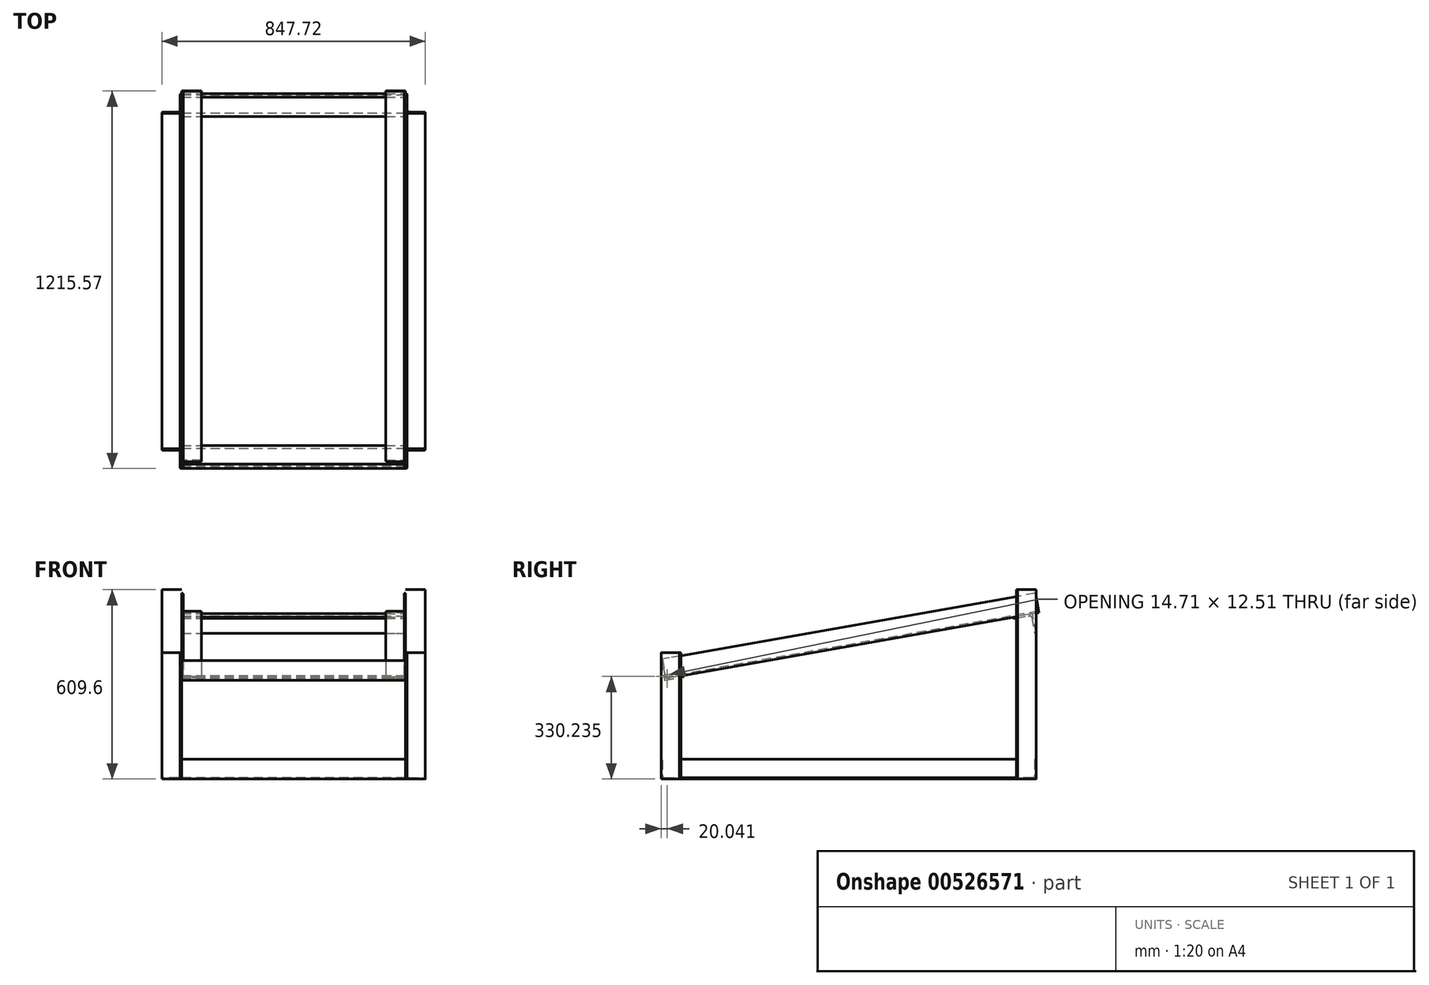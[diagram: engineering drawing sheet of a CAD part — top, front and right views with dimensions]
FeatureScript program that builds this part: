
annotation { "Feature Type Name" : "Feature", "Feature Type Description" : "" }
export const myFeature = defineFeature(function(context is Context, id is Id, definition is map)
    precondition{}
    {
        {
            var Q0;
            Q0=qCreatedBy(makeId("Right.planeOp"),FACE);
            var sketch = newSketch(context, id + "F0", { "sketchPlane" : qUnion([Q0])});
            skLineSegment(sketch, "E0.bottom", {"start": v(0, 0) * mm, "end": v(63.5, 0) * mm});
            skLineSegment(sketch, "E0.top", {"start": v(0, 406.4) * mm, "end": v(63.5, 406.4) * mm});
            skLineSegment(sketch, "E0.left", {"start": v(0, 0) * mm, "end": v(0, 406.4) * mm});
            skLineSegment(sketch, "E0.right", {"start": v(63.5, 0) * mm, "end": v(63.5, 406.4) * mm});
            skLineSegment(sketch, "E1.bottom", {"start": v(1143, 0) * mm, "end": v(1206.5, 0) * mm});
            skLineSegment(sketch, "E1.top", {"start": v(1143, 609.6) * mm, "end": v(1206.5, 609.6) * mm});
            skLineSegment(sketch, "E1.left", {"start": v(1143, 0) * mm, "end": v(1143, 609.6) * mm});
            skLineSegment(sketch, "E1.right", {"start": v(1206.5, 0) * mm, "end": v(1206.5, 609.6) * mm});
            skLineSegment(sketch, "E2", {"start": v(66.78, 468.54) * mm, "end": v(1142.38, 658.2) * mm, "construction": true});
            skLineSegment(sketch, "E3", {"start": v(66.78, 468.54) * mm, "end": v(-8.2, 893.78) * mm, "construction": true});
            skLineSegment(sketch, "E4", {"start": v(-8.2, 893.78) * mm, "end": v(1067.4, 1083.44) * mm, "construction": true});
            skLineSegment(sketch, "E5", {"start": v(1067.4, 1083.44) * mm, "end": v(1142.38, 658.2) * mm, "construction": true});
            skLineSegment(sketch, "E6", {"start": v(21.14, 325.08) * mm, "end": v(1234.33, 539) * mm});
            skLineSegment(sketch, "E7", {"start": v(1234.33, 539) * mm, "end": v(1208.97, 682.83) * mm});
            skLineSegment(sketch, "E8", {"start": v(1208.97, 682.83) * mm, "end": v(-4.22, 468.92) * mm});
            skLineSegment(sketch, "E9", {"start": v(-4.22, 468.92) * mm, "end": v(21.14, 325.08) * mm});
            skLineSegment(sketch, "E10", {"start": v(5.24, 378.7) * mm, "end": v(13.79, 330.24) * mm});
            skLineSegment(sketch, "E11", {"start": v(21.14, 325.08) * mm, "end": v(69.6, 333.63) * mm});
            skLineSegment(sketch, "E12", {"start": v(73.29, 331.05) * mm, "end": v(73.56, 329.5) * mm});
            skLineSegment(sketch, "E13", {"start": v(73.56, 329.5) * mm, "end": v(11.03, 318.46) * mm});
            skLineSegment(sketch, "E14", {"start": v(11.03, 318.46) * mm, "end": v(0, 381) * mm});
            skLineSegment(sketch, "E15", {"start": v(0, 381) * mm, "end": v(1.56, 381.28) * mm});
            skPoint(sketch, "E16.visualSharp", {"position": v(14.89, 323.98) * mm});
            skArc(sketch, "E16.filletArc", {"start": v(13.79, 330.24) * mm, "mid": v(16.4, 326.14) * mm, "end": v(21.14, 325.08) * mm});
            skPoint(sketch, "E17.visualSharp", {"position": v(72.73, 334.18) * mm});
            skArc(sketch, "E17.filletArc", {"start": v(73.29, 331.05) * mm, "mid": v(71.98, 333.1) * mm, "end": v(69.6, 333.63) * mm});
            skPoint(sketch, "E18.visualSharp", {"position": v(4.7, 381.83) * mm});
            skArc(sketch, "E18.filletArc", {"start": v(5.24, 378.7) * mm, "mid": v(3.94, 380.75) * mm, "end": v(1.56, 381.28) * mm});
            skLineSegment(sketch, "E19", {"start": v(1132.94, 521.12) * mm, "end": v(1195.47, 532.15) * mm});
            skLineSegment(sketch, "E20", {"start": v(1195.47, 532.15) * mm, "end": v(1206.5, 469.62) * mm});
            skLineSegment(sketch, "E21", {"start": v(1206.5, 469.62) * mm, "end": v(1204.94, 469.34) * mm});
            skLineSegment(sketch, "E22", {"start": v(1201.26, 471.92) * mm, "end": v(1192.71, 520.38) * mm});
            skLineSegment(sketch, "E23", {"start": v(1185.36, 525.53) * mm, "end": v(1136.9, 516.99) * mm});
            skLineSegment(sketch, "E24", {"start": v(1133.21, 519.56) * mm, "end": v(1132.94, 521.12) * mm});
            skPoint(sketch, "E25.visualSharp", {"position": v(1133.77, 516.43) * mm});
            skArc(sketch, "E25.filletArc", {"start": v(1133.21, 519.56) * mm, "mid": v(1134.52, 517.51) * mm, "end": v(1136.9, 516.99) * mm});
            skPoint(sketch, "E26.visualSharp", {"position": v(1201.8, 468.79) * mm});
            skArc(sketch, "E26.filletArc", {"start": v(1201.26, 471.92) * mm, "mid": v(1202.56, 469.87) * mm, "end": v(1204.94, 469.34) * mm});
            skPoint(sketch, "E27.visualSharp", {"position": v(1191.61, 526.63) * mm});
            skArc(sketch, "E27.filletArc", {"start": v(1192.71, 520.38) * mm, "mid": v(1190.1, 524.48) * mm, "end": v(1185.36, 525.53) * mm});
            skLineSegment(sketch, "E28", {"start": v(-4.22, 468.92) * mm, "end": v(-16.35, 537.7) * mm, "construction": true});
            skLineSegment(sketch, "E29", {"start": v(-16.35, 537.7) * mm, "end": v(52.44, 549.83) * mm, "construction": true});
            skLineSegment(sketch, "E30", {"start": v(1208.97, 682.83) * mm, "end": v(1196.84, 751.62) * mm, "construction": true});
            skLineSegment(sketch, "E31", {"start": v(1196.84, 751.62) * mm, "end": v(1128.05, 739.5) * mm, "construction": true});
            skLineSegment(sketch, "E32", {"start": v(63.5, 0) * mm, "end": v(1143, 0) * mm, "construction": true});
            skLineSegment(sketch, "E33", {"start": v(603.25, 0) * mm, "end": v(603.25, 427.73) * mm, "construction": true});
            skSolve(sketch);
        }
        {
            var Q0;
            Q0=qCreatedBy(makeId("Top.planeOp"),FACE);
            var sketch = newSketch(context, id + "F1", { "sketchPlane" : qUnion([Q0])});
            skLineSegment(sketch, "E34", {"start": v(-355.6, 0) * mm, "end": v(355.6, 0) * mm, "construction": true});
            skLineSegment(sketch, "E35", {"start": v(360.36, 0) * mm, "end": v(360.36, 63.5) * mm});
            skLineSegment(sketch, "E36", {"start": v(360.36, 63.5) * mm, "end": v(423.86, 63.5) * mm});
            skLineSegment(sketch, "E37", {"start": v(423.86, 63.5) * mm, "end": v(423.86, 61.91) * mm});
            skLineSegment(sketch, "E38", {"start": v(420.69, 58.74) * mm, "end": v(371.48, 58.74) * mm});
            skLineSegment(sketch, "E39", {"start": v(365.13, 52.39) * mm, "end": v(365.13, 3.17) * mm});
            skLineSegment(sketch, "E40", {"start": v(361.95, 0) * mm, "end": v(360.36, 0) * mm});
            skPoint(sketch, "E41.visualSharp", {"position": v(365.13, 58.74) * mm});
            skArc(sketch, "E41.filletArc", {"start": v(371.48, 58.74) * mm, "mid": v(366.98, 56.88) * mm, "end": v(365.13, 52.39) * mm});
            skPoint(sketch, "E42.visualSharp", {"position": v(423.86, 58.74) * mm});
            skArc(sketch, "E42.filletArc", {"start": v(420.69, 58.74) * mm, "mid": v(422.93, 59.67) * mm, "end": v(423.86, 61.91) * mm});
            skPoint(sketch, "E43.visualSharp", {"position": v(365.13, 0) * mm});
            skArc(sketch, "E43.filletArc", {"start": v(361.95, 0) * mm, "mid": v(364.2, 0.93) * mm, "end": v(365.13, 3.17) * mm});
            skLineSegment(sketch, "E44", {"start": v(0, 603.25) * mm, "end": v(711.2, 603.25) * mm, "construction": true});
            skLineSegment(sketch, "E45.MirrorCS", {"start": v(361.95, 1206.5) * mm, "end": v(360.36, 1206.5) * mm});
            skLineSegment(sketch, "E46.MirrorCS", {"start": v(423.86, 1143) * mm, "end": v(423.86, 1144.59) * mm});
            skArc(sketch, "E47.MirrorCS", {"start": v(420.69, 1147.76) * mm, "mid": v(422.93, 1146.83) * mm, "end": v(423.86, 1144.59) * mm});
            skArc(sketch, "E48.MirrorCS", {"start": v(361.95, 1206.5) * mm, "mid": v(364.2, 1205.57) * mm, "end": v(365.13, 1203.33) * mm});
            skArc(sketch, "E49.MirrorCS", {"start": v(371.48, 1147.76) * mm, "mid": v(366.98, 1149.62) * mm, "end": v(365.13, 1154.11) * mm});
            skLineSegment(sketch, "E50.MirrorCS", {"start": v(365.13, 1154.11) * mm, "end": v(365.13, 1203.33) * mm});
            skLineSegment(sketch, "E51.MirrorCS", {"start": v(420.69, 1147.76) * mm, "end": v(371.48, 1147.76) * mm});
            skLineSegment(sketch, "E52.MirrorCS", {"start": v(360.36, 1206.5) * mm, "end": v(360.36, 1143) * mm});
            skLineSegment(sketch, "E53.MirrorCS", {"start": v(360.36, 1143) * mm, "end": v(423.86, 1143) * mm});
            skPoint(sketch, "E54.MirrorP", {"position": v(365.13, 1147.76) * mm});
            skPoint(sketch, "E55.MirrorP", {"position": v(423.86, 1147.76) * mm});
            skPoint(sketch, "E56.MirrorP", {"position": v(365.13, 1206.5) * mm});
            skLineSegment(sketch, "E57.MirrorCS", {"start": v(-361.95, 1206.5) * mm, "end": v(-360.36, 1206.5) * mm});
            skLineSegment(sketch, "E58.MirrorCS", {"start": v(-423.86, 1143) * mm, "end": v(-423.86, 1144.59) * mm});
            skArc(sketch, "E59.MirrorCS", {"start": v(-361.95, 1206.5) * mm, "mid": v(-364.2, 1205.57) * mm, "end": v(-365.13, 1203.33) * mm});
            skArc(sketch, "E60.MirrorCS", {"start": v(-420.69, 1147.76) * mm, "mid": v(-422.93, 1146.83) * mm, "end": v(-423.86, 1144.59) * mm});
            skArc(sketch, "E61.MirrorCS", {"start": v(-371.48, 1147.76) * mm, "mid": v(-366.98, 1149.62) * mm, "end": v(-365.13, 1154.11) * mm});
            skPoint(sketch, "E62.MirrorP", {"position": v(-423.86, 1147.76) * mm});
            skLineSegment(sketch, "E63.MirrorCS", {"start": v(-420.69, 1147.76) * mm, "end": v(-371.48, 1147.76) * mm});
            skLineSegment(sketch, "E64.MirrorCS", {"start": v(-360.36, 1143) * mm, "end": v(-423.86, 1143) * mm});
            skPoint(sketch, "E65.MirrorP", {"position": v(-365.13, 1147.76) * mm});
            skPoint(sketch, "E66.MirrorP", {"position": v(-365.13, 1206.5) * mm});
            skLineSegment(sketch, "E67.MirrorCS", {"start": v(-365.13, 1154.11) * mm, "end": v(-365.13, 1203.33) * mm});
            skLineSegment(sketch, "E68.MirrorCS", {"start": v(-360.36, 1206.5) * mm, "end": v(-360.36, 1143) * mm});
            skLineSegment(sketch, "E69.MirrorCS", {"start": v(-361.95, 0) * mm, "end": v(-360.36, 0) * mm});
            skLineSegment(sketch, "E70.MirrorCS", {"start": v(-423.86, 63.5) * mm, "end": v(-423.86, 61.91) * mm});
            skArc(sketch, "E71.MirrorCS", {"start": v(-420.69, 58.74) * mm, "mid": v(-422.93, 59.67) * mm, "end": v(-423.86, 61.91) * mm});
            skArc(sketch, "E72.MirrorCS", {"start": v(-361.95, 0) * mm, "mid": v(-364.2, 0.93) * mm, "end": v(-365.13, 3.17) * mm});
            skArc(sketch, "E73.MirrorCS", {"start": v(-371.48, 58.74) * mm, "mid": v(-366.98, 56.88) * mm, "end": v(-365.13, 52.39) * mm});
            skLineSegment(sketch, "E74.MirrorCS", {"start": v(-365.13, 52.39) * mm, "end": v(-365.13, 3.17) * mm});
            skLineSegment(sketch, "E75.MirrorCS", {"start": v(-420.69, 58.74) * mm, "end": v(-371.48, 58.74) * mm});
            skLineSegment(sketch, "E76.MirrorCS", {"start": v(-360.36, 0) * mm, "end": v(-360.36, 63.5) * mm});
            skLineSegment(sketch, "E77.MirrorCS", {"start": v(-360.36, 63.5) * mm, "end": v(-423.86, 63.5) * mm});
            skPoint(sketch, "E78.MirrorP", {"position": v(-365.13, 58.74) * mm});
            skPoint(sketch, "E79.MirrorP", {"position": v(-423.86, 58.74) * mm});
            skPoint(sketch, "E80.MirrorP", {"position": v(-365.13, 0) * mm});
            skSolve(sketch);
        }
        {
            var Q0;
            Q0=makeQuery(id+"F1.imprint","IMPRINT",FACE,{"disambiguationData":[TD([[makeQuery(id+"F1.imprint","IMPRINT",EDGE,{"derivedFrom":sQuery(id+"F1.wireOp",EDGE,"E69.MirrorCS")}),1.0]])]});
            var Q1;
            Q1=makeQuery(id+"F1.imprint","IMPRINT",FACE,{"disambiguationData":[TD([[makeQuery(id+"F1.imprint","IMPRINT",EDGE,{"derivedFrom":sQuery(id+"F1.wireOp",EDGE,"E35")}),-1.0]])]});
            extrude(context, id + "F2", {"entities" : qUnion([Q0, Q1]), "depth" : 406.4 * mm, "offsetDistance" : 25.4 * mm});
        }
        {
            var Q0;
            Q0=makeQuery(id+"F1.imprint","IMPRINT",FACE,{"disambiguationData":[TD([[makeQuery(id+"F1.imprint","IMPRINT",EDGE,{"derivedFrom":sQuery(id+"F1.wireOp",EDGE,"E57.MirrorCS")}),-1.0]])]});
            var Q1;
            Q1=makeQuery(id+"F1.imprint","IMPRINT",FACE,{"disambiguationData":[TD([[makeQuery(id+"F1.imprint","IMPRINT",EDGE,{"derivedFrom":sQuery(id+"F1.wireOp",EDGE,"E45.MirrorCS")}),1.0]])]});
            extrude(context, id + "F3", {"entities" : qUnion([Q0, Q1]), "depth" : 609.6 * mm, "offsetDistance" : 25.4 * mm});
        }
        {
            var Q0;
            Q0=makeQuery(id+"F0.imprint","IMPRINT",FACE,{"disambiguationData":[TD([[makeQuery(id+"F0.imprint","IMPRINT",EDGE,{"derivedFrom":sQuery(id+"F0.wireOp",EDGE,"E10")}),-1.0]])]});
            var Q1;
            {var subQ0=sQuery(id+"F0.wireOp",EDGE,"E20");Q1=makeQuery(id+"F0.imprint","IMPRINT",FACE,{"disambiguationData":[TD([[makeQuery(id+"F0.imprint","IMPRINT",EDGE,{"derivedFrom":subQ0}),-1.0]])]});}
            var Q2;
            {var subQ1=sQuery(id+"F0.wireOp",EDGE,"E12");Q2=makeQuery(id+"F0.imprint","IMPRINT",FACE,{"disambiguationData":[TD([[makeQuery(id+"F0.imprint","IMPRINT",EDGE,{"derivedFrom":subQ1}),-1.0]])]});}
            var Q3;
            {var subQ4=sQuery(id+"F0.wireOp",EDGE,"E24");Q3=makeQuery(id+"F0.imprint","IMPRINT",FACE,{"disambiguationData":[TD([[makeQuery(id+"F0.imprint","IMPRINT",EDGE,{"derivedFrom":subQ4}),-1.0]])]});}
            var Q4;
            Q4=makeQuery(id+"F3.opExtrude","SWEPT_FACE",FACE,{"disambiguationData":[OSD([sQuery(id+"F1.wireOp",EDGE,"E68.MirrorCS")])]});
            var Q5;
            Q5=makeQuery(id+"F3.opExtrude","SWEPT_FACE",FACE,{"disambiguationData":[OSD([sQuery(id+"F1.wireOp",EDGE,"E52.MirrorCS")])]});
            extrude(context, id + "F4", {"entities" : qUnion([Q0, Q1, Q2, Q3]), "endBound" : BoundingType.UP_TO_SURFACE, "oppositeDirection" : true, "depth" : 25.4 * mm, "endBoundEntityFace" : qUnion([Q4]), "offsetDistance" : 25.4 * mm, "hasSecondDirection" : true, "secondDirectionBound" : SecondDirectionBoundingType.UP_TO_SURFACE, "secondDirectionOppositeDirection" : false, "secondDirectionDepth" : 25.4 * mm, "secondDirectionBoundEntityFace" : qUnion([Q5])});
        }
        {
            var Q0;
            Q0=makeQuery(id+"F4.opExtrude","SWEPT_FACE",FACE,{"disambiguationData":[OSD([sQuery(id+"F0.wireOp",EDGE,"E10")])]});
            var sketch = newSketch(context, id + "F5", { "sketchPlane" : qUnion([Q0])});
            skLineSegment(sketch, "E81", {"start": v(-360.36, 379.97) * mm, "end": v(-360.36, 316.47) * mm});
            skLineSegment(sketch, "E82", {"start": v(-360.36, 316.47) * mm, "end": v(-296.86, 316.47) * mm});
            skLineSegment(sketch, "E83", {"start": v(-296.86, 316.47) * mm, "end": v(-296.86, 318.06) * mm});
            skLineSegment(sketch, "E84", {"start": v(-300.04, 321.24) * mm, "end": v(-349.25, 321.24) * mm});
            skLineSegment(sketch, "E85", {"start": v(-355.6, 327.59) * mm, "end": v(-355.6, 376.8) * mm});
            skLineSegment(sketch, "E86", {"start": v(-358.77, 379.97) * mm, "end": v(-360.36, 379.97) * mm});
            skPoint(sketch, "E87.visualSharp", {"position": v(-355.6, 379.97) * mm});
            skArc(sketch, "E87.filletArc", {"start": v(-355.6, 376.8) * mm, "mid": v(-356.53, 379.04) * mm, "end": v(-358.77, 379.97) * mm});
            skPoint(sketch, "E88.visualSharp", {"position": v(-296.86, 321.24) * mm});
            skArc(sketch, "E88.filletArc", {"start": v(-296.86, 318.06) * mm, "mid": v(-297.8, 320.3) * mm, "end": v(-300.04, 321.24) * mm});
            skPoint(sketch, "E89.visualSharp", {"position": v(-355.6, 321.24) * mm});
            skArc(sketch, "E89.filletArc", {"start": v(-355.6, 327.59) * mm, "mid": v(-353.74, 323.1) * mm, "end": v(-349.25, 321.24) * mm});
            skSolve(sketch);
        }
        {
            var Q0;
            Q0=qSketchRegion(id+"F5",true);
            extrude(context, id + "F6", {"entities" : qUnion([Q0]), "depth" : 1219.2 * mm, "offsetDistance" : 25.4 * mm});
        }
        {
            var Q0;
            Q0=makeQuery(id+"F6.opExtrude","SWEPT_FACE",FACE,{"disambiguationData":[OSD([sQuery(id+"F5.wireOp",EDGE,"E81")])]});
            var sketch = newSketch(context, id + "F7", { "sketchPlane" : qUnion([Q0])});
            skLineSegment(sketch, "E90", {"start": v(14.89, 323.98) * mm, "end": v(27.4, 326.19) * mm});
            skLineSegment(sketch, "E91", {"start": v(27.4, 326.19) * mm, "end": v(12.68, 336.49) * mm});
            skLineSegment(sketch, "E92", {"start": v(12.68, 336.49) * mm, "end": v(14.89, 323.98) * mm});
            skSolve(sketch);
        }
        {
            var Q0;
            Q0=qSketchRegion(id+"F7",true);
            extrude(context, id + "F8", {"entities" : qUnion([Q0]), "operationType" : NewBodyOperationType.REMOVE, "endBound" : BoundingType.THROUGH_ALL, "oppositeDirection" : true, "depth" : 25.4 * mm, "offsetDistance" : 25.4 * mm});
        }
        {
            var Q0;
            Q0=makeQuery(id+"F6.opExtrude","SWEPT_BODY",BODY,{"disambiguationData":[OSD([sQuery(id+"F5.wireOp",EDGE,"E81"),sQuery(id+"F5.wireOp",EDGE,"E82"),sQuery(id+"F5.wireOp",EDGE,"E83"),sQuery(id+"F5.wireOp",EDGE,"E84"),sQuery(id+"F5.wireOp",EDGE,"E85"),sQuery(id+"F5.wireOp",EDGE,"E86"),sQuery(id+"F5.wireOp",EDGE,"E87.filletArc"),sQuery(id+"F5.wireOp",EDGE,"E88.filletArc"),sQuery(id+"F5.wireOp",EDGE,"E89.filletArc")])]});
            var Q1;
            Q1=qCreatedBy(makeId("Right.planeOp"),FACE);
            mirror(context, id + "F9", {"entities" : qUnion([Q0]), "mirrorPlane" : qUnion([Q1])});
        }
        {
            var Q0;
            Q0=qCreatedBy(makeId("Right.planeOp"),FACE);
            var sketch = newSketch(context, id + "F10", { "sketchPlane" : qUnion([Q0])});
            skLineSegment(sketch, "E93", {"start": v(0, 63.5) * mm, "end": v(0, 0) * mm});
            skLineSegment(sketch, "E94", {"start": v(0, 0) * mm, "end": v(63.5, 0) * mm});
            skLineSegment(sketch, "E95", {"start": v(63.5, 0) * mm, "end": v(63.5, 1.59) * mm});
            skLineSegment(sketch, "E96", {"start": v(60.33, 4.76) * mm, "end": v(11.11, 4.76) * mm});
            skLineSegment(sketch, "E97", {"start": v(4.76, 11.11) * mm, "end": v(4.76, 60.33) * mm});
            skLineSegment(sketch, "E98", {"start": v(1.59, 63.5) * mm, "end": v(0, 63.5) * mm});
            skPoint(sketch, "E99.visualSharp", {"position": v(4.76, 63.5) * mm});
            skArc(sketch, "E99.filletArc", {"start": v(4.76, 60.33) * mm, "mid": v(3.83, 62.57) * mm, "end": v(1.59, 63.5) * mm});
            skPoint(sketch, "E100.visualSharp", {"position": v(63.5, 4.76) * mm});
            skArc(sketch, "E100.filletArc", {"start": v(63.5, 1.59) * mm, "mid": v(62.57, 3.83) * mm, "end": v(60.33, 4.76) * mm});
            skPoint(sketch, "E101.visualSharp", {"position": v(4.76, 4.76) * mm});
            skArc(sketch, "E101.filletArc", {"start": v(4.76, 11.11) * mm, "mid": v(6.62, 6.62) * mm, "end": v(11.11, 4.76) * mm});
            skLineSegment(sketch, "E102.MirrorCS", {"start": v(1143, 0) * mm, "end": v(1143, 1.59) * mm});
            skArc(sketch, "E103.MirrorCS", {"start": v(1143, 1.59) * mm, "mid": v(1143.93, 3.83) * mm, "end": v(1146.17, 4.76) * mm});
            skLineSegment(sketch, "E104.MirrorCS", {"start": v(1204.91, 63.5) * mm, "end": v(1206.5, 63.5) * mm});
            skArc(sketch, "E105.MirrorCS", {"start": v(1201.74, 60.33) * mm, "mid": v(1202.67, 62.57) * mm, "end": v(1204.91, 63.5) * mm});
            skArc(sketch, "E106.MirrorCS", {"start": v(1201.74, 11.11) * mm, "mid": v(1199.88, 6.62) * mm, "end": v(1195.39, 4.76) * mm});
            skLineSegment(sketch, "E107.MirrorCS", {"start": v(1206.5, 63.5) * mm, "end": v(1206.5, 0) * mm});
            skLineSegment(sketch, "E108.MirrorCS", {"start": v(1206.5, 0) * mm, "end": v(1143, 0) * mm});
            skLineSegment(sketch, "E109.MirrorCS", {"start": v(1201.74, 11.11) * mm, "end": v(1201.74, 60.33) * mm});
            skLineSegment(sketch, "E110.MirrorCS", {"start": v(1146.17, 4.76) * mm, "end": v(1195.39, 4.76) * mm});
            skPoint(sketch, "E111.MirrorP", {"position": v(1143, 4.76) * mm});
            skPoint(sketch, "E112.MirrorP", {"position": v(1201.74, 4.76) * mm});
            skPoint(sketch, "E113.MirrorP", {"position": v(1201.74, 63.5) * mm});
            skSolve(sketch);
        }
        {
            var Q0;
            Q0=qSketchRegion(id+"F10",true);
            var Q1;
            Q1=makeQuery(id+"F2.opExtrude","SWEPT_FACE",FACE,{"disambiguationData":[OSD([sQuery(id+"F1.wireOp",EDGE,"E35")])]});
            var Q2;
            Q2=makeQuery(id+"F2.opExtrude","SWEPT_FACE",FACE,{"disambiguationData":[OSD([sQuery(id+"F1.wireOp",EDGE,"E76.MirrorCS")])]});
            extrude(context, id + "F11", {"entities" : qUnion([Q0]), "endBound" : BoundingType.UP_TO_SURFACE, "depth" : 25.4 * mm, "endBoundEntityFace" : qUnion([Q1]), "offsetDistance" : 25.4 * mm, "hasSecondDirection" : true, "secondDirectionBound" : SecondDirectionBoundingType.UP_TO_SURFACE, "secondDirectionOppositeDirection" : true, "secondDirectionDepth" : 25.4 * mm, "secondDirectionBoundEntityFace" : qUnion([Q2])});
        }
        {
            var Q0;
            Q0=makeQuery(id+"F3.opExtrude","SWEPT_FACE",FACE,{"disambiguationData":[OSD([sQuery(id+"F1.wireOp",EDGE,"E53.MirrorCS")])]});
            var sketch = newSketch(context, id + "F12", { "sketchPlane" : qUnion([Q0])});
            skLineSegment(sketch, "E114", {"start": v(360.36, 63.5) * mm, "end": v(360.36, 0) * mm});
            skLineSegment(sketch, "E115", {"start": v(360.36, 0) * mm, "end": v(423.86, 0) * mm});
            skLineSegment(sketch, "E116", {"start": v(423.86, 0) * mm, "end": v(423.86, 1.59) * mm});
            skLineSegment(sketch, "E117", {"start": v(420.69, 4.76) * mm, "end": v(371.48, 4.76) * mm});
            skLineSegment(sketch, "E118", {"start": v(365.13, 11.11) * mm, "end": v(365.13, 60.33) * mm});
            skLineSegment(sketch, "E119", {"start": v(361.95, 63.5) * mm, "end": v(360.36, 63.5) * mm});
            skPoint(sketch, "E120.visualSharp", {"position": v(365.13, 63.5) * mm});
            skArc(sketch, "E120.filletArc", {"start": v(365.13, 60.33) * mm, "mid": v(364.2, 62.57) * mm, "end": v(361.95, 63.5) * mm});
            skPoint(sketch, "E121.visualSharp", {"position": v(423.86, 4.76) * mm});
            skArc(sketch, "E121.filletArc", {"start": v(423.86, 1.59) * mm, "mid": v(422.93, 3.83) * mm, "end": v(420.69, 4.76) * mm});
            skPoint(sketch, "E122.visualSharp", {"position": v(365.13, 4.76) * mm});
            skArc(sketch, "E122.filletArc", {"start": v(365.13, 11.11) * mm, "mid": v(366.98, 6.62) * mm, "end": v(371.48, 4.76) * mm});
            skLineSegment(sketch, "E123.MirrorCS", {"start": v(-423.86, 0) * mm, "end": v(-423.86, 1.59) * mm});
            skLineSegment(sketch, "E124.MirrorCS", {"start": v(-361.95, 63.5) * mm, "end": v(-360.36, 63.5) * mm});
            skArc(sketch, "E125.MirrorCS", {"start": v(-365.13, 60.33) * mm, "mid": v(-364.2, 62.57) * mm, "end": v(-361.95, 63.5) * mm});
            skArc(sketch, "E126.MirrorCS", {"start": v(-423.86, 1.59) * mm, "mid": v(-422.93, 3.83) * mm, "end": v(-420.69, 4.76) * mm});
            skArc(sketch, "E127.MirrorCS", {"start": v(-365.13, 11.11) * mm, "mid": v(-366.98, 6.62) * mm, "end": v(-371.48, 4.76) * mm});
            skLineSegment(sketch, "E128.MirrorCS", {"start": v(-365.13, 11.11) * mm, "end": v(-365.13, 60.33) * mm});
            skLineSegment(sketch, "E129.MirrorCS", {"start": v(-420.69, 4.76) * mm, "end": v(-371.48, 4.76) * mm});
            skLineSegment(sketch, "E130.MirrorCS", {"start": v(-360.36, 63.5) * mm, "end": v(-360.36, 0) * mm});
            skLineSegment(sketch, "E131.MirrorCS", {"start": v(-360.36, 0) * mm, "end": v(-423.86, 0) * mm});
            skPoint(sketch, "E132.MirrorP", {"position": v(-365.13, 4.76) * mm});
            skPoint(sketch, "E133.MirrorP", {"position": v(-365.13, 63.5) * mm});
            skPoint(sketch, "E134.MirrorP", {"position": v(-423.86, 4.76) * mm});
            skSolve(sketch);
        }
        {
            var Q0;
            Q0=qSketchRegion(id+"F12",true);
            var Q1;
            Q1=makeQuery(id+"F2.opExtrude","SWEPT_FACE",FACE,{"disambiguationData":[OSD([sQuery(id+"F1.wireOp",EDGE,"E36")])]});
            extrude(context, id + "F13", {"entities" : qUnion([Q0]), "endBound" : BoundingType.UP_TO_SURFACE, "depth" : 25.4 * mm, "endBoundEntityFace" : qUnion([Q1]), "offsetDistance" : 25.4 * mm});
        }
        {
            var Q0;
            Q0=makeQuery(id+"F4.opExtrude","SWEPT_FACE",FACE,{"disambiguationData":[OSD([sQuery(id+"F0.wireOp",EDGE,"E10")])]});
            var sketch = newSketch(context, id + "F14", { "sketchPlane" : qUnion([Q0])});
            skLineSegment(sketch, "E135", {"start": v(-360.36, 321.24) * mm, "end": v(-296.86, 321.24) * mm});
            skLineSegment(sketch, "E136", {"start": v(-360.36, 321.24) * mm, "end": v(-360.36, 257.74) * mm});
            skLineSegment(sketch, "E137", {"start": v(-296.86, 316.47) * mm, "end": v(-296.86, 321.24) * mm});
            skLineSegment(sketch, "E138", {"start": v(-360.36, 257.74) * mm, "end": v(-355.6, 257.74) * mm});
            skLineSegment(sketch, "E139", {"start": v(-355.6, 257.74) * mm, "end": v(-355.6, 316.47) * mm});
            skLineSegment(sketch, "E140", {"start": v(-355.6, 316.47) * mm, "end": v(-296.86, 316.47) * mm});
            skSolve(sketch);
        }
        {
            var Q0;
            Q0=makeQuery(id+"F4.opExtrude","SWEPT_FACE",FACE,{"disambiguationData":[OSD([sQuery(id+"F0.wireOp",EDGE,"E11")])]});
            var sketch = newSketch(context, id + "F15", { "sketchPlane" : qUnion([Q0])});
            skLineSegment(sketch, "E141.bottom", {"start": v(354.01, 129.66) * mm, "end": v(360.36, 129.66) * mm});
            skLineSegment(sketch, "E141.top", {"start": v(354.01, 77.27) * mm, "end": v(360.36, 77.27) * mm});
            skLineSegment(sketch, "E141.left", {"start": v(354.01, 129.66) * mm, "end": v(354.01, 77.27) * mm});
            skLineSegment(sketch, "E141.right", {"start": v(360.36, 129.66) * mm, "end": v(360.36, 77.27) * mm});
            skLineSegment(sketch, "E142.bottom", {"start": v(360.36, 1258.6) * mm, "end": v(354.01, 1258.6) * mm});
            skLineSegment(sketch, "E142.top", {"start": v(360.36, 1206.22) * mm, "end": v(354.01, 1206.22) * mm});
            skLineSegment(sketch, "E142.left", {"start": v(360.36, 1258.6) * mm, "end": v(360.36, 1206.22) * mm});
            skLineSegment(sketch, "E142.right", {"start": v(354.01, 1258.6) * mm, "end": v(354.01, 1206.22) * mm});
            skSolve(sketch);
        }
    });
